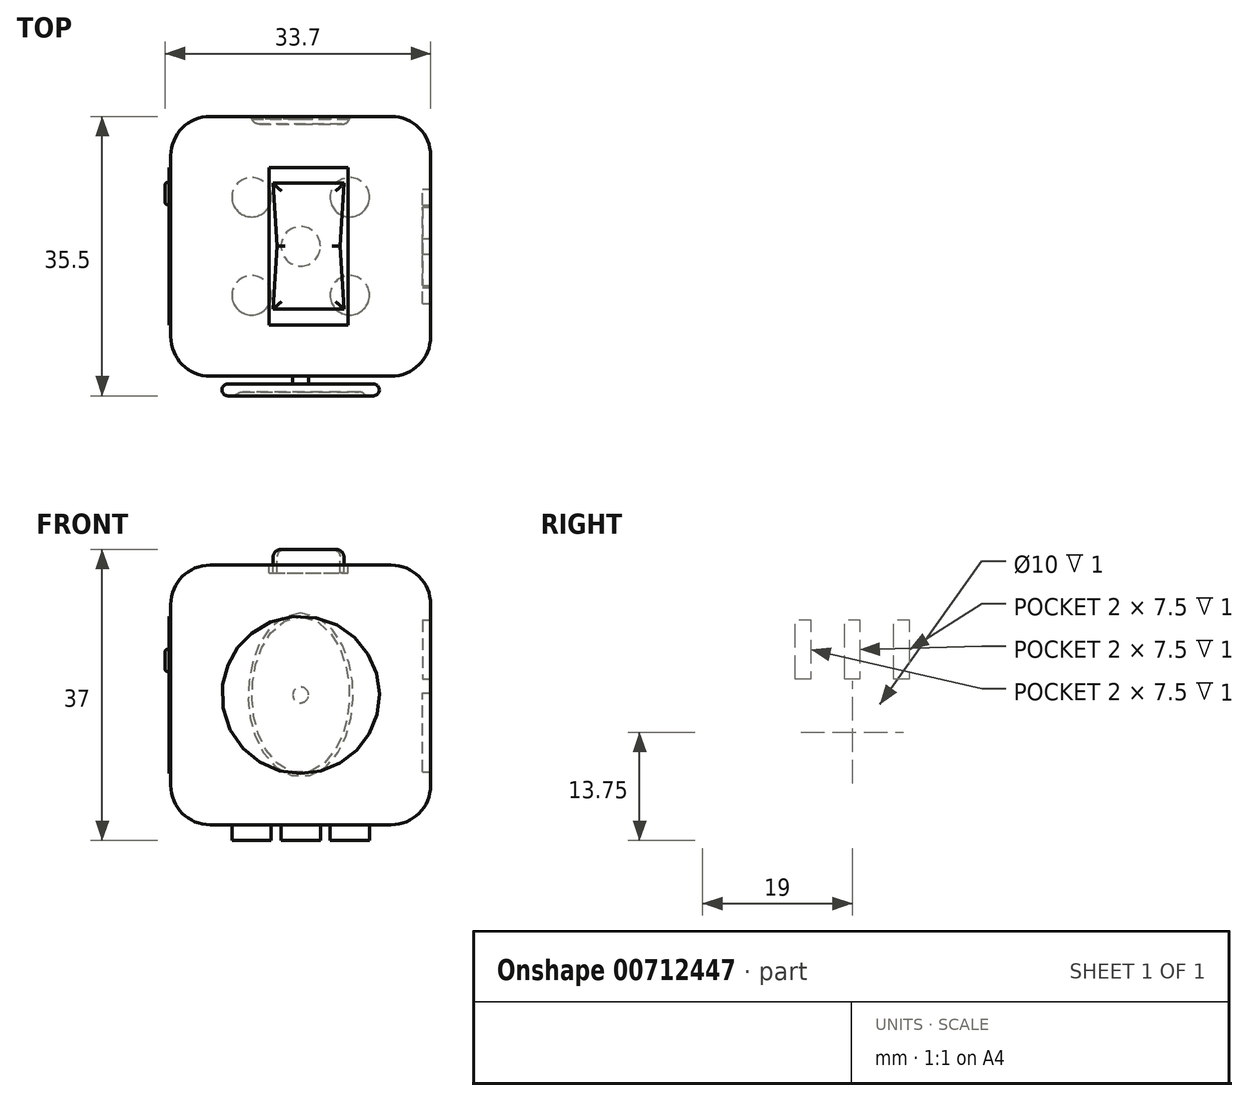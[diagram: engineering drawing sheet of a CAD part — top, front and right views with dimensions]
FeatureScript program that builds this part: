
annotation { "Feature Type Name" : "Feature", "Feature Type Description" : "" }
export const myFeature = defineFeature(function(context is Context, id is Id, definition is map)
    precondition{}
    {
        {
            var Q0;
            Q0=qCreatedBy(makeId("Front.planeOp"),FACE);
            var sketch = newSketch(context, id + "F0", { "sketchPlane" : qUnion([Q0])});
            skPoint(sketch, "E0.0", {"position": v(0, 0) * mm});
            skLineSegment(sketch, "E1.bottom", {"start": v(0, 0) * mm, "end": v(33, 0) * mm});
            skLineSegment(sketch, "E1.top", {"start": v(0, 33) * mm, "end": v(33, 33) * mm});
            skLineSegment(sketch, "E1.left", {"start": v(0, 0) * mm, "end": v(0, 33) * mm});
            skLineSegment(sketch, "E1.right", {"start": v(33, 0) * mm, "end": v(33, 33) * mm});
            skSolve(sketch);
        }
        {
            var Q0;
            Q0=makeQuery(id+"F0.imprint","IMPRINT",FACE,{"disambiguationData":[TD([[makeQuery(id+"F0.imprint","IMPRINT",EDGE,{"derivedFrom":sQuery(id+"F0.wireOp",EDGE,"E1.bottom")}),1.0]])]});
            extrude(context, id + "F1", {"entities" : qUnion([Q0]), "depth" : 33 * mm, "offsetDistance" : 25 * mm});
        }
        {
            var Q0;
            Q0=makeQuery(id+"F1.opExtrude","SWEPT_EDGE",EDGE,{"disambiguationData":[OSD([sQuery(id+"F0.wireOp",EDGE,"E1.top"),sQuery(id+"F0.wireOp",EDGE,"E1.right")])]});
            var Q1;
            Q1=makeQuery(id+"F1.opExtrude","CAP_EDGE",EDGE,{"disambiguationData":[OSD([sQuery(id+"F0.wireOp",EDGE,"E1.top")])],"isStart":false});
            var Q2;
            Q2=makeQuery(id+"F1.opExtrude","SWEPT_EDGE",EDGE,{"disambiguationData":[OSD([sQuery(id+"F0.wireOp",EDGE,"E1.top"),sQuery(id+"F0.wireOp",EDGE,"E1.left")])]});
            var Q3;
            Q3=makeQuery(id+"F1.opExtrude","CAP_EDGE",EDGE,{"disambiguationData":[OSD([sQuery(id+"F0.wireOp",EDGE,"E1.top")])],"isStart":true});
            var Q4;
            Q4=makeQuery(id+"F1.opExtrude","CAP_EDGE",EDGE,{"disambiguationData":[OSD([sQuery(id+"F0.wireOp",EDGE,"E1.right")])],"isStart":true});
            var Q5;
            Q5=makeQuery(id+"F1.opExtrude","CAP_EDGE",EDGE,{"disambiguationData":[OSD([sQuery(id+"F0.wireOp",EDGE,"E1.right")])],"isStart":false});
            var Q6;
            Q6=makeQuery(id+"F1.opExtrude","CAP_EDGE",EDGE,{"disambiguationData":[OSD([sQuery(id+"F0.wireOp",EDGE,"E1.left")])],"isStart":false});
            var Q7;
            Q7=makeQuery(id+"F1.opExtrude","CAP_EDGE",EDGE,{"disambiguationData":[OSD([sQuery(id+"F0.wireOp",EDGE,"E1.left")])],"isStart":true});
            var Q8;
            Q8=makeQuery(id+"F1.opExtrude","SWEPT_EDGE",EDGE,{"disambiguationData":[OSD([sQuery(id+"F0.wireOp",EDGE,"E1.bottom"),sQuery(id+"F0.wireOp",EDGE,"E1.left")])]});
            var Q9;
            Q9=makeQuery(id+"F1.opExtrude","CAP_EDGE",EDGE,{"disambiguationData":[OSD([sQuery(id+"F0.wireOp",EDGE,"E1.bottom")])],"isStart":false});
            var Q10;
            Q10=makeQuery(id+"F1.opExtrude","SWEPT_EDGE",EDGE,{"disambiguationData":[OSD([sQuery(id+"F0.wireOp",EDGE,"E1.bottom"),sQuery(id+"F0.wireOp",EDGE,"E1.right")])]});
            var Q11;
            Q11=makeQuery(id+"F1.opExtrude","CAP_EDGE",EDGE,{"disambiguationData":[OSD([sQuery(id+"F0.wireOp",EDGE,"E1.bottom")])],"isStart":true});
            fillet(context, id + "F2", {"entities" : qUnion([Q0, Q1, Q2, Q3, Q4, Q5, Q6, Q7, Q8, Q9, Q10, Q11]), "radius" : 5 * mm, "tangentPropagation" : true, "allowEdgeOverflow" : false});
        }
        {
            var Q0;
            Q0=makeQuery(id+"F1.opExtrude","SWEPT_FACE",FACE,{"disambiguationData":[OSD([sQuery(id+"F0.wireOp",EDGE,"E1.right")])]});
            var sketch = newSketch(context, id + "F3", { "sketchPlane" : qUnion([Q0])});
            skLineSegment(sketch, "E2.bottom", {"start": v(-23.75, 26) * mm, "end": v(-21.75, 26) * mm});
            skLineSegment(sketch, "E2.top", {"start": v(-23.75, 18.5) * mm, "end": v(-21.75, 18.5) * mm});
            skLineSegment(sketch, "E2.left", {"start": v(-23.75, 26) * mm, "end": v(-23.75, 18.5) * mm});
            skLineSegment(sketch, "E2.right", {"start": v(-21.75, 26) * mm, "end": v(-21.75, 18.5) * mm});
            skLineSegment(sketch, "E3.bottom", {"start": v(-17.5, 26) * mm, "end": v(-15.5, 26) * mm});
            skLineSegment(sketch, "E3.top", {"start": v(-17.5, 18.5) * mm, "end": v(-15.5, 18.5) * mm});
            skLineSegment(sketch, "E3.left", {"start": v(-17.5, 26) * mm, "end": v(-17.5, 18.5) * mm});
            skLineSegment(sketch, "E3.right", {"start": v(-15.5, 26) * mm, "end": v(-15.5, 18.5) * mm});
            skLineSegment(sketch, "E4.bottom", {"start": v(-11.25, 26) * mm, "end": v(-9.25, 26) * mm});
            skLineSegment(sketch, "E4.top", {"start": v(-11.25, 18.5) * mm, "end": v(-9.25, 18.5) * mm});
            skLineSegment(sketch, "E4.left", {"start": v(-11.25, 26) * mm, "end": v(-11.25, 18.5) * mm});
            skLineSegment(sketch, "E4.right", {"start": v(-9.25, 26) * mm, "end": v(-9.25, 18.5) * mm});
            skCircle(sketch, "E5", {"center": v(-16.5, 11.75) * mm, "radius": 5 * mm});
            skPoint(sketch, "E6", {"position": v(-16.5, 18.5) * mm});
            skSolve(sketch);
        }
        {
            var Q0;
            Q0=makeQuery(id+"F3.imprint","IMPRINT",FACE,{"disambiguationData":[TD([[makeQuery(id+"F3.imprint","IMPRINT",EDGE,{"derivedFrom":sQuery(id+"F3.wireOp",EDGE,"E2.bottom")}),-1.0]])]});
            var Q1;
            Q1=makeQuery(id+"F3.imprint","IMPRINT",FACE,{"disambiguationData":[TD([[makeQuery(id+"F3.imprint","IMPRINT",EDGE,{"derivedFrom":sQuery(id+"F3.wireOp",EDGE,"E3.bottom")}),-1.0]])]});
            var Q2;
            Q2=makeQuery(id+"F3.imprint","IMPRINT",FACE,{"disambiguationData":[TD([[makeQuery(id+"F3.imprint","IMPRINT",EDGE,{"derivedFrom":sQuery(id+"F3.wireOp",EDGE,"E4.bottom")}),-1.0]])]});
            extrude(context, id + "F4", {"entities" : qUnion([Q0, Q1, Q2]), "operationType" : NewBodyOperationType.REMOVE, "oppositeDirection" : true, "depth" : 1 * mm, "offsetDistance" : 25 * mm});
        }
        {
            var Q0;
            Q0=makeQuery(id+"F3.imprint","IMPRINT",FACE,{"disambiguationData":[TD([[makeQuery(id+"F3.imprint","IMPRINT",EDGE,{"derivedFrom":sQuery(id+"F3.wireOp",EDGE,"E5")}),1.0]])]});
            extrude(context, id + "F5", {"entities" : qUnion([Q0]), "operationType" : NewBodyOperationType.REMOVE, "oppositeDirection" : true, "depth" : 1 * mm, "offsetDistance" : 25 * mm});
        }
        {
            var Q0;
            Q0=makeQuery(id+"F1.opExtrude","CAP_FACE",FACE,{"disambiguationData":[OSD([sQuery(id+"F0.wireOp",EDGE,"E1.bottom"),sQuery(id+"F0.wireOp",EDGE,"E1.top"),sQuery(id+"F0.wireOp",EDGE,"E1.left"),sQuery(id+"F0.wireOp",EDGE,"E1.right")])],"isStart":true});
            var sketch = newSketch(context, id + "F6", { "sketchPlane" : qUnion([Q0])});
            skEllipse(sketch, "E7", {"center": v(-16.5, 16.5) * mm, "majorRadius": 10 * mm, "minorRadius": 6.25 * mm, "majorAxis": v(0, 1)});
            skPoint(sketch, "E8", {"position": v(-16.5, 28) * mm});
            skPoint(sketch, "E9", {"position": v(-16.5, 26.5) * mm});
            skPoint(sketch, "E10", {"position": v(-16.5, 6.5) * mm});
            skSolve(sketch);
        }
        {
            var Q0;
            Q0=makeQuery(id+"F6.imprint","IMPRINT",FACE,{"disambiguationData":[TD([[makeQuery(id+"F6.imprint","IMPRINT",EDGE,{"derivedFrom":sQuery(id+"F6.wireOp",EDGE,"E7")}),1.0]])]});
            extrude(context, id + "F7", {"entities" : qUnion([Q0]), "operationType" : NewBodyOperationType.REMOVE, "oppositeDirection" : true, "depth" : 1 * mm, "offsetDistance" : 25 * mm});
        }
        {
            var Q0;
            Q0=makeQuery(id+"F7.boolean.opBoolean","COPY",EDGE,{"derivedFrom":makeQuery(id+"F7.opExtrude","CAP_EDGE",EDGE,{"disambiguationData":[OSD([sQuery(id+"F6.wireOp",EDGE,"E7")])],"isStart":false})});
            fillet(context, id + "F8", {"entities" : qUnion([Q0]), "radius" : 1 * mm, "tangentPropagation" : true, "allowEdgeOverflow" : false});
        }
        {
            var Q0;
            Q0=makeQuery(id+"F8.opFillet","BLEND_EDGE",EDGE,{"blendedFrom":[makeQuery(id+"F7.boolean.opBoolean","COPY",EDGE,{"derivedFrom":makeQuery(id+"F7.opExtrude","CAP_EDGE",EDGE,{"disambiguationData":[OSD([sQuery(id+"F6.wireOp",EDGE,"E7")])],"isStart":false})}),makeQuery(id+"F1.opExtrude","CAP_FACE",FACE,{"disambiguationData":[OSD([sQuery(id+"F0.wireOp",EDGE,"E1.bottom"),sQuery(id+"F0.wireOp",EDGE,"E1.top"),sQuery(id+"F0.wireOp",EDGE,"E1.left"),sQuery(id+"F0.wireOp",EDGE,"E1.right")])],"isStart":true})],"blendedInto":[makeQuery(id+"F1.opExtrude","CAP_FACE",FACE,{"disambiguationData":[OSD([sQuery(id+"F0.wireOp",EDGE,"E1.bottom"),sQuery(id+"F0.wireOp",EDGE,"E1.top"),sQuery(id+"F0.wireOp",EDGE,"E1.left"),sQuery(id+"F0.wireOp",EDGE,"E1.right")])],"isStart":true})]});
            fillet(context, id + "F9", {"entities" : qUnion([Q0]), "radius" : .5 * mm, "tangentPropagation" : true, "allowEdgeOverflow" : false});
        }
        {
            var Q0;
            Q0=makeQuery(id+"F1.opExtrude","CAP_FACE",FACE,{"disambiguationData":[OSD([sQuery(id+"F0.wireOp",EDGE,"E1.bottom"),sQuery(id+"F0.wireOp",EDGE,"E1.top"),sQuery(id+"F0.wireOp",EDGE,"E1.left"),sQuery(id+"F0.wireOp",EDGE,"E1.right")])],"isStart":false});
            var sketch = newSketch(context, id + "F10", { "sketchPlane" : qUnion([Q0])});
            skPoint(sketch, "E11", {"position": v(16.5, 28) * mm});
            skPoint(sketch, "E12", {"position": v(5, 16.5) * mm});
            skCircle(sketch, "E13", {"center": v(16.5, 16.5) * mm, "radius": 1 * mm});
            skSolve(sketch);
        }
        {
            var Q0;
            Q0=makeQuery(id+"F10.imprint","IMPRINT",FACE,{"disambiguationData":[TD([[makeQuery(id+"F10.imprint","IMPRINT",EDGE,{"derivedFrom":sQuery(id+"F10.wireOp",EDGE,"E13")}),1.0]])]});
            extrude(context, id + "F11", {"entities" : qUnion([Q0]), "operationType" : NewBodyOperationType.ADD, "depth" : 1 * mm, "offsetDistance" : 25 * mm});
        }
        {
            var Q0;
            Q0=makeQuery(id+"F11.opExtrude","CAP_FACE",FACE,{"disambiguationData":[OSD([sQuery(id+"F10.wireOp",EDGE,"E13")])],"isStart":false});
            var sketch = newSketch(context, id + "F12", { "sketchPlane" : qUnion([Q0])});
            skCircle(sketch, "E14", {"center": v(16.5, 16.5) * mm, "radius": 10 * mm});
            skSolve(sketch);
        }
        {
            var Q0;
            Q0=makeQuery(id+"F12.imprint","IMPRINT",FACE,{"disambiguationData":[TD([[makeQuery(id+"F12.imprint","IMPRINT",EDGE,{"derivedFrom":sQuery(id+"F12.wireOp",EDGE,"E14")}),1.0]])]});
            var Q1;
            Q1=makeQuery(id+"F12.imprint","IMPRINT",FACE,{"disambiguationData":[TD([[makeQuery(id+"F12.imprint","IMPRINT",EDGE,{"derivedFrom":makeQuery(id+"F11.opExtrude","CAP_EDGE",EDGE,{"disambiguationData":[OSD([sQuery(id+"F10.wireOp",EDGE,"E13")])],"isStart":false})}),1.0]])]});
            extrude(context, id + "F13", {"entities" : qUnion([Q0, Q1]), "operationType" : NewBodyOperationType.ADD, "depth" : 1.5 * mm, "offsetDistance" : 25 * mm});
        }
        {
            var Q0;
            Q0=makeQuery(id+"F13.opExtrude","CAP_EDGE",EDGE,{"disambiguationData":[OSD([sQuery(id+"F12.wireOp",EDGE,"E14")])],"isStart":true});
            var Q1;
            Q1=makeQuery(id+"F13.opExtrude","CAP_EDGE",EDGE,{"disambiguationData":[OSD([sQuery(id+"F12.wireOp",EDGE,"E14")])],"isStart":false});
            fillet(context, id + "F14", {"entities" : qUnion([Q0, Q1]), "radius" : .75 * mm, "tangentPropagation" : true, "allowEdgeOverflow" : false});
        }
        {
            var Q0;
            Q0=makeQuery(id+"F13.opExtrude","CAP_FACE",FACE,{"disambiguationData":[OSD([sQuery(id+"F12.wireOp",EDGE,"E14")])],"isStart":false});
            var sketch = newSketch(context, id + "F15", { "sketchPlane" : qUnion([Q0])});
            skCircle(sketch, "E15", {"center": v(16.5, 16.5) * mm, "radius": 8.25 * mm});
            skSolve(sketch);
        }
        {
            var Q0;
            Q0=makeQuery(id+"F15.imprint","IMPRINT",FACE,{"disambiguationData":[TD([[makeQuery(id+"F15.imprint","IMPRINT",EDGE,{"derivedFrom":sQuery(id+"F15.wireOp",EDGE,"E15")}),1.0]])]});
            extrude(context, id + "F16", {"entities" : qUnion([Q0]), "operationType" : NewBodyOperationType.REMOVE, "oppositeDirection" : true, "depth" : .5 * mm, "offsetDistance" : 25 * mm});
        }
        {
            var Q0;
            Q0=makeQuery(id+"F16.boolean.opBoolean","COPY",EDGE,{"derivedFrom":makeQuery(id+"F16.opExtrude","CAP_EDGE",EDGE,{"disambiguationData":[OSD([sQuery(id+"F15.wireOp",EDGE,"E15")])],"isStart":false})});
            fillet(context, id + "F17", {"entities" : qUnion([Q0]), "radius" : 1 * mm, "tangentPropagation" : true, "allowEdgeOverflow" : false});
        }
        {
            var Q0;
            Q0=makeQuery(id+"F17.opFillet","BLEND_EDGE",EDGE,{"blendedFrom":[makeQuery(id+"F16.boolean.opBoolean","COPY",EDGE,{"derivedFrom":makeQuery(id+"F16.opExtrude","CAP_EDGE",EDGE,{"disambiguationData":[OSD([sQuery(id+"F15.wireOp",EDGE,"E15")])],"isStart":false})}),makeQuery(id+"F13.opExtrude","CAP_FACE",FACE,{"disambiguationData":[OSD([sQuery(id+"F12.wireOp",EDGE,"E14")])],"isStart":false})],"blendedInto":[makeQuery(id+"F13.opExtrude","CAP_FACE",FACE,{"disambiguationData":[OSD([sQuery(id+"F12.wireOp",EDGE,"E14")])],"isStart":false})]});
            fillet(context, id + "F18", {"entities" : qUnion([Q0]), "radius" : 1 * mm, "tangentPropagation" : true, "allowEdgeOverflow" : false});
        }
        {
            var Q0;
            Q0=makeQuery(id+"F1.opExtrude","SWEPT_FACE",FACE,{"disambiguationData":[OSD([sQuery(id+"F0.wireOp",EDGE,"E1.bottom")])]});
            var sketch = newSketch(context, id + "F19", { "sketchPlane" : qUnion([Q0])});
            skCircle(sketch, "E16", {"center": v(16.5, 16.5) * mm, "radius": 2.5 * mm});
            skCircle(sketch, "E17", {"center": v(22.73, 22.73) * mm, "radius": 2.5 * mm});
            skCircle(sketch, "E18", {"center": v(22.73, 10.27) * mm, "radius": 2.5 * mm});
            skCircle(sketch, "E19", {"center": v(10.27, 22.73) * mm, "radius": 2.5 * mm});
            skCircle(sketch, "E20", {"center": v(10.27, 10.27) * mm, "radius": 2.5 * mm});
            skSolve(sketch);
        }
        {
            var Q0;
            Q0=makeQuery(id+"F19.imprint","IMPRINT",FACE,{"disambiguationData":[TD([[makeQuery(id+"F19.imprint","IMPRINT",EDGE,{"derivedFrom":sQuery(id+"F19.wireOp",EDGE,"E17")}),1.0]])]});
            var Q1;
            Q1=makeQuery(id+"F19.imprint","IMPRINT",FACE,{"disambiguationData":[TD([[makeQuery(id+"F19.imprint","IMPRINT",EDGE,{"derivedFrom":sQuery(id+"F19.wireOp",EDGE,"E16")}),1.0]])]});
            var Q2;
            Q2=makeQuery(id+"F19.imprint","IMPRINT",FACE,{"disambiguationData":[TD([[makeQuery(id+"F19.imprint","IMPRINT",EDGE,{"derivedFrom":sQuery(id+"F19.wireOp",EDGE,"E18")}),1.0]])]});
            var Q3;
            Q3=makeQuery(id+"F19.imprint","IMPRINT",FACE,{"disambiguationData":[TD([[makeQuery(id+"F19.imprint","IMPRINT",EDGE,{"derivedFrom":sQuery(id+"F19.wireOp",EDGE,"E20")}),1.0]])]});
            var Q4;
            Q4=makeQuery(id+"F19.imprint","IMPRINT",FACE,{"disambiguationData":[TD([[makeQuery(id+"F19.imprint","IMPRINT",EDGE,{"derivedFrom":sQuery(id+"F19.wireOp",EDGE,"E19")}),1.0]])]});
            extrude(context, id + "F20", {"entities" : qUnion([Q0, Q1, Q2, Q3, Q4]), "operationType" : NewBodyOperationType.ADD, "depth" : 2 * mm, "offsetDistance" : 25 * mm});
        }
        {
            var Q0;
            Q0=makeQuery(id+"F1.opExtrude","SWEPT_FACE",FACE,{"disambiguationData":[OSD([sQuery(id+"F0.wireOp",EDGE,"E1.top")])]});
            var sketch = newSketch(context, id + "F21", { "sketchPlane" : qUnion([Q0])});
            skLineSegment(sketch, "E21.bottom", {"start": v(12.5, -26.5) * mm, "end": v(22.5, -26.5) * mm});
            skLineSegment(sketch, "E21.top", {"start": v(12.5, -6.5) * mm, "end": v(22.5, -6.5) * mm});
            skLineSegment(sketch, "E21.left", {"start": v(12.5, -26.5) * mm, "end": v(12.5, -6.5) * mm});
            skLineSegment(sketch, "E21.right", {"start": v(22.5, -26.5) * mm, "end": v(22.5, -6.5) * mm});
            skLineSegment(sketch, "E22", {"start": v(22, -24.5) * mm, "end": v(13, -24.5) * mm});
            skLineSegment(sketch, "E23", {"start": v(13, -24.5) * mm, "end": v(13.5, -16.5) * mm});
            skLineSegment(sketch, "E24", {"start": v(13.5, -16.5) * mm, "end": v(13, -8.5) * mm});
            skLineSegment(sketch, "E25", {"start": v(13, -8.5) * mm, "end": v(22, -8.5) * mm});
            skLineSegment(sketch, "E26", {"start": v(22, -8.5) * mm, "end": v(21.5, -16.5) * mm});
            skLineSegment(sketch, "E27", {"start": v(21.5, -16.5) * mm, "end": v(22, -24.5) * mm});
            skLineSegment(sketch, "E28", {"start": v(12.5, -16.5) * mm, "end": v(22.5, -16.5) * mm});
            skSolve(sketch);
        }
        {
            var Q0;
            {var subQ1=sQuery(id+"F21.wireOp",EDGE,"E21.bottom");Q0=makeQuery(id+"F21.imprint","IMPRINT",FACE,{"disambiguationData":[TD([[makeQuery(id+"F21.imprint","IMPRINT",EDGE,{"derivedFrom":subQ1}),1.0]])]});}
            var Q1;
            {var subQ1=sQuery(id+"F21.wireOp",EDGE,"E21.top");Q1=makeQuery(id+"F21.imprint","IMPRINT",FACE,{"disambiguationData":[TD([[makeQuery(id+"F21.imprint","IMPRINT",EDGE,{"derivedFrom":subQ1}),-1.0]])]});}
            extrude(context, id + "F22", {"entities" : qUnion([Q0, Q1]), "operationType" : NewBodyOperationType.REMOVE, "oppositeDirection" : true, "depth" : 1 * mm, "offsetDistance" : 25 * mm});
        }
        {
            var Q0;
            Q0=makeQuery(id+"F22.boolean.opBoolean","SPLIT",FACE,{"disambiguationData":[TD([makeQuery(id+"F22.opExtrude","SWEPT_FACE",FACE,{"disambiguationData":[OSD([sQuery(id+"F21.wireOp",EDGE,"E22")])]})])],"derivedFrom":makeQuery(id+"F1.opExtrude","SWEPT_FACE",FACE,{"disambiguationData":[OSD([sQuery(id+"F0.wireOp",EDGE,"E1.top")])]})});
            extrude(context, id + "F23", {"entities" : qUnion([Q0]), "operationType" : NewBodyOperationType.ADD, "depth" : 2 * mm, "offsetDistance" : 25 * mm});
        }
        {
            var Q0;
            Q0=makeQuery(id+"F23.opExtrude","CAP_EDGE",EDGE,{"disambiguationData":[OSD([sQuery(id+"F21.wireOp",EDGE,"E26")])],"isStart":false});
            var Q1;
            Q1=makeQuery(id+"F23.opExtrude","CAP_EDGE",EDGE,{"disambiguationData":[OSD([sQuery(id+"F21.wireOp",EDGE,"E27")])],"isStart":false});
            var Q2;
            Q2=makeQuery(id+"F23.opExtrude","CAP_EDGE",EDGE,{"disambiguationData":[OSD([sQuery(id+"F21.wireOp",EDGE,"E25")])],"isStart":false});
            var Q3;
            Q3=makeQuery(id+"F23.opExtrude","CAP_EDGE",EDGE,{"disambiguationData":[OSD([sQuery(id+"F21.wireOp",EDGE,"E24")])],"isStart":false});
            var Q4;
            Q4=makeQuery(id+"F23.opExtrude","CAP_EDGE",EDGE,{"disambiguationData":[OSD([sQuery(id+"F21.wireOp",EDGE,"E23")])],"isStart":false});
            var Q5;
            Q5=makeQuery(id+"F23.opExtrude","CAP_EDGE",EDGE,{"disambiguationData":[OSD([sQuery(id+"F21.wireOp",EDGE,"E22")])],"isStart":false});
            fillet(context, id + "F24", {"entities" : qUnion([Q0, Q1, Q2, Q3, Q4, Q5]), "radius" : 1 * mm, "tangentPropagation" : true, "allowEdgeOverflow" : false});
        }
        {
            var Q0;
            Q0=makeQuery(id+"F1.opExtrude","SWEPT_FACE",FACE,{"disambiguationData":[OSD([sQuery(id+"F0.wireOp",EDGE,"E1.left")])]});
            var sketch = newSketch(context, id + "F25", { "sketchPlane" : qUnion([Q0])});
            skCircle(sketch, "E29", {"center": v(16.5, 16.5) * mm, "radius": 10 * mm});
            skPoint(sketch, "E30", {"position": v(9.8, 20.88) * mm});
            skCircle(sketch, "E31", {"center": v(9.8, 20.88) * mm, "radius": 1.38 * mm});
            skSolve(sketch);
        }
        {
            var Q0;
            Q0=makeQuery(id+"F25.imprint","IMPRINT",FACE,{"disambiguationData":[TD([[makeQuery(id+"F25.imprint","IMPRINT",EDGE,{"derivedFrom":sQuery(id+"F25.wireOp",EDGE,"E29")}),1.0]])]});
            extrude(context, id + "F26", {"entities" : qUnion([Q0]), "operationType" : NewBodyOperationType.ADD, "depth" : .2 * mm, "offsetDistance" : 25 * mm});
        }
        {
            var Q0;
            Q0=makeQuery(id+"F26.boolean.opBoolean","SPLIT",FACE,{"disambiguationData":[TD([makeQuery(id+"F26.opExtrude","SWEPT_FACE",FACE,{"disambiguationData":[OSD([sQuery(id+"F25.wireOp",EDGE,"E31")])]})])],"derivedFrom":makeQuery(id+"F1.opExtrude","SWEPT_FACE",FACE,{"disambiguationData":[OSD([sQuery(id+"F0.wireOp",EDGE,"E1.left")])]})});
            extrude(context, id + "F27", {"entities" : qUnion([Q0]), "operationType" : NewBodyOperationType.ADD, "depth" : .7 * mm, "offsetDistance" : 25 * mm});
        }
        {
            var Q0;
            Q0=makeQuery(id+"F27.opExtrude","CAP_EDGE",EDGE,{"disambiguationData":[OSD([sQuery(id+"F25.wireOp",EDGE,"E31")])],"isStart":false});
            fillet(context, id + "F28", {"entities" : qUnion([Q0]), "radius" : .2 * mm, "tangentPropagation" : true, "allowEdgeOverflow" : false});
        }
    });
